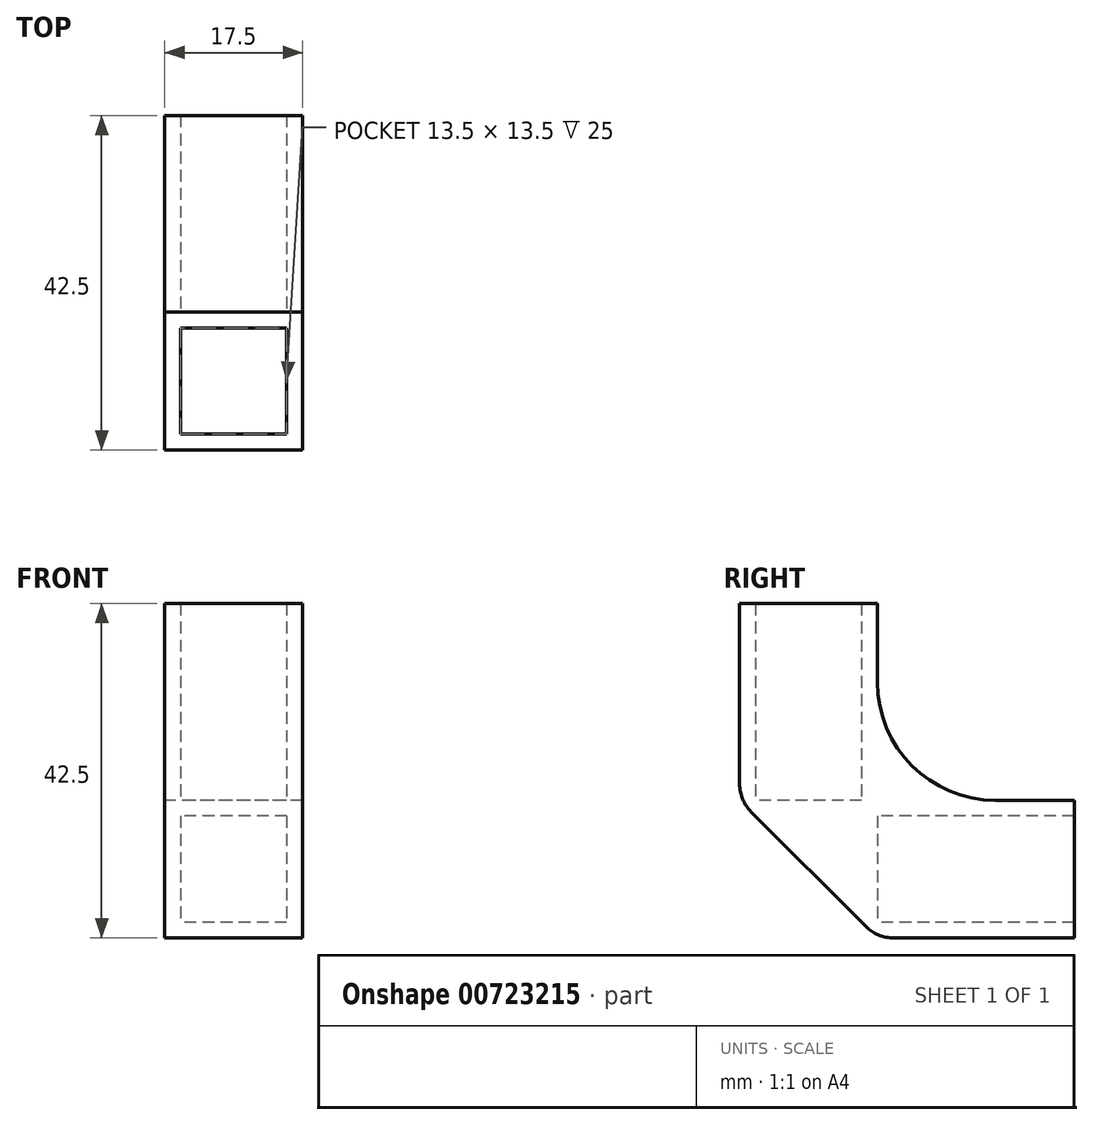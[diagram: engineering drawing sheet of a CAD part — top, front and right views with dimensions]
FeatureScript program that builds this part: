
annotation { "Feature Type Name" : "Feature", "Feature Type Description" : "" }
export const myFeature = defineFeature(function(context is Context, id is Id, definition is map)
    precondition{}
    {
        {
            var Q0;
            Q0=qCreatedBy(makeId("Top.planeOp"),FACE);
            var sketch = newSketch(context, id + "F0", { "sketchPlane" : qUnion([Q0])});
            skLineSegment(sketch, "E0.bottom", {"start": v(8.75, 8.75) * mm, "end": v(-8.75, 8.75) * mm});
            skLineSegment(sketch, "E0.top", {"start": v(8.75, -8.75) * mm, "end": v(-8.75, -8.75) * mm});
            skLineSegment(sketch, "E0.left", {"start": v(8.75, 8.75) * mm, "end": v(8.75, -8.75) * mm});
            skLineSegment(sketch, "E0.right", {"start": v(-8.75, 8.75) * mm, "end": v(-8.75, -8.75) * mm});
            skPoint(sketch, "E0.middle", {"position": v(0, 0) * mm});
            skLineSegment(sketch, "E1.bottom", {"start": v(6.75, 6.75) * mm, "end": v(-6.75, 6.75) * mm});
            skLineSegment(sketch, "E1.top", {"start": v(6.75, -6.75) * mm, "end": v(-6.75, -6.75) * mm});
            skLineSegment(sketch, "E1.left", {"start": v(6.75, 6.75) * mm, "end": v(6.75, -6.75) * mm});
            skLineSegment(sketch, "E1.right", {"start": v(-6.75, 6.75) * mm, "end": v(-6.75, -6.75) * mm});
            skSolve(sketch);
        }
        {
            var Q0;
            Q0=qCreatedBy(makeId("Top.planeOp"),FACE);
            var sketch = newSketch(context, id + "F1", { "sketchPlane" : qUnion([Q0])});
            skLineSegment(sketch, "E2.bottom", {"start": v(8.75, 8.75) * mm, "end": v(-8.75, 8.75) * mm});
            skLineSegment(sketch, "E2.top", {"start": v(8.75, -8.75) * mm, "end": v(-8.75, -8.75) * mm});
            skLineSegment(sketch, "E2.left", {"start": v(8.75, 8.75) * mm, "end": v(8.75, -8.75) * mm});
            skLineSegment(sketch, "E2.right", {"start": v(-8.75, 8.75) * mm, "end": v(-8.75, -8.75) * mm});
            skPoint(sketch, "E2.middle", {"position": v(0, 0) * mm});
            skLineSegment(sketch, "E3.bottom", {"start": v(6.75, 6.75) * mm, "end": v(-6.75, 6.75) * mm});
            skLineSegment(sketch, "E3.top", {"start": v(6.75, -6.75) * mm, "end": v(-6.75, -6.75) * mm});
            skLineSegment(sketch, "E3.left", {"start": v(6.75, 6.75) * mm, "end": v(6.75, -6.75) * mm});
            skLineSegment(sketch, "E3.right", {"start": v(-6.75, 6.75) * mm, "end": v(-6.75, -6.75) * mm});
            skSolve(sketch);
        }
        {
            var Q0;
            Q0 = qSketchRegion(id + "F1", true);
            extrude(context, id + "F2", {"entities" : qUnion([Q0]), "depth" : 25 * mm, "offsetDistance" : 25 * mm});
        }
        {
            var Q0;
            Q0=makeQuery(id+"F2.opExtrude","SWEPT_FACE",FACE,{"disambiguationData":[OSD([sQuery(id+"F1.wireOp",EDGE,"E2.bottom")])]});
            var sketch = newSketch(context, id + "F3", { "sketchPlane" : qUnion([Q0])});
            skLineSegment(sketch, "E4.bottom", {"start": v(-8.75, 0) * mm, "end": v(8.75, 0) * mm});
            skLineSegment(sketch, "E4.top", {"start": v(-8.75, -17.5) * mm, "end": v(8.75, -17.5) * mm});
            skLineSegment(sketch, "E4.left", {"start": v(-8.75, 0) * mm, "end": v(-8.75, -17.5) * mm});
            skLineSegment(sketch, "E4.right", {"start": v(8.75, 0) * mm, "end": v(8.75, -17.5) * mm});
            skLineSegment(sketch, "E5.bottom", {"start": v(-6.75, -2) * mm, "end": v(6.75, -2) * mm});
            skLineSegment(sketch, "E5.top", {"start": v(-6.75, -15.5) * mm, "end": v(6.75, -15.5) * mm});
            skLineSegment(sketch, "E5.left", {"start": v(-6.75, -2) * mm, "end": v(-6.75, -15.5) * mm});
            skLineSegment(sketch, "E5.right", {"start": v(6.75, -2) * mm, "end": v(6.75, -15.5) * mm});
            skPoint(sketch, "E5.middle", {"position": v(0, -8.75) * mm});
            skSolve(sketch);
        }
        {
            var Q0;
            Q0 = qSketchRegion(id + "F3", true);
            extrude(context, id + "F4", {"entities" : qUnion([Q0]), "depth" : 25 * mm, "offsetDistance" : 25 * mm});
        }
        {
            var Q0;
            Q0=makeQuery(id+"F4.opExtrude","SWEPT_FACE",FACE,{"disambiguationData":[OSD([sQuery(id+"F3.wireOp",EDGE,"E4.right")])]});
            var sketch = newSketch(context, id + "F5", { "sketchPlane" : qUnion([Q0])});
            skLineSegment(sketch, "E6", {"start": v(-8.75, -17.5) * mm, "end": v(8.75, 0) * mm});
            skLineSegment(sketch, "E7", {"start": v(8.75, 0) * mm, "end": v(-8.75, 0) * mm});
            skLineSegment(sketch, "E8", {"start": v(-8.75, 0) * mm, "end": v(-8.75, -17.5) * mm});
            skSolve(sketch);
        }
        {
            var Q0;
            Q0 = qSketchRegion(id + "F5", true);
            var Q1;
            Q1=makeQuery(id+"F4.opExtrude","SWEPT_FACE",FACE,{"disambiguationData":[OSD([sQuery(id+"F3.wireOp",EDGE,"E4.left")])]});
            extrude(context, id + "F6", {"entities" : qUnion([Q0]), "operationType" : NewBodyOperationType.ADD, "endBound" : BoundingType.UP_TO_SURFACE, "oppositeDirection" : true, "depth" : 25 * mm, "endBoundEntityFace" : qUnion([Q1]), "offsetDistance" : 25 * mm});
        }
        {
            var Q0;
            Q0=makeQuery(id+"F6.boolean.opBoolean","MERGE",EDGE,{"derivedFrom":[makeQuery(id+"F2.opExtrude","CAP_EDGE",EDGE,{"disambiguationData":[OSD([sQuery(id+"F1.wireOp",EDGE,"E2.top")])],"isStart":true}),makeQuery(id+"F6.opExtrude","SWEPT_EDGE",EDGE,{"disambiguationData":[OSD([sQuery(id+"F5.wireOp",EDGE,"E6"),sQuery(id+"F5.wireOp",EDGE,"E7")])]})]});
            var Q1;
            {var subQ0=sQuery(id+"F3.wireOp",EDGE,"E4.top");Q1=makeQuery(id+"F6.boolean.opBoolean","MERGE",EDGE,{"derivedFrom":[makeQuery(id+"F4.opExtrude","CAP_EDGE",EDGE,{"disambiguationData":[OSD([subQ0])],"isStart":true}),makeQuery(id+"F6.opExtrude","SWEPT_EDGE",EDGE,{"disambiguationData":[OSD([subQ0,sQuery(id+"F3.wireOp",EDGE,"E4.right"),sQuery(id+"F5.wireOp",EDGE,"E6"),sQuery(id+"F5.wireOp",EDGE,"E8")])]})]});}
            fillet(context, id + "F7", {"entities" : qUnion([Q0, Q1]), "radius" : 5 * mm, "tangentPropagation" : true, "allowEdgeOverflow" : false});
        }
        {
            var Q0;
            Q0=makeQuery(id+"F2.opExtrude","CAP_EDGE",EDGE,{"disambiguationData":[OSD([sQuery(id+"F1.wireOp",EDGE,"E2.bottom")])],"isStart":true});
            fillet(context, id + "F8", {"entities" : qUnion([Q0]), "radius" : 15 * mm, "tangentPropagation" : true, "allowEdgeOverflow" : false});
        }
    });
